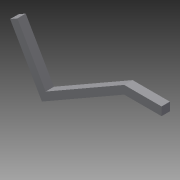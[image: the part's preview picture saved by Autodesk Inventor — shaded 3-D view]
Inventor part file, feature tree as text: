
AUTODESK INVENTOR PART (.ipt)
format: ipt  version: 2013 (Build 170138000, 138)  size: 73,728 bytes
history: native  units: in
note: dims shown in document units (in); Inventor stores cm internally (conversion verified against a paired STEP export)
features: extrude x1, sketch x1
ambient origin geometry x8: Origin, YZ Plane, XZ Plane, XY Plane, X Axis, Y Axis, Z Axis, Center Point
bodies: Solid1 (feature_tree)
feature tree (2):
  extrude  "Extrusion1"  Depth=1.0in
  sketch  "Sketch1"  dims[d0=1.0in d1=1.0in d2=1.0in d3=1.0in d4=0.0in]
